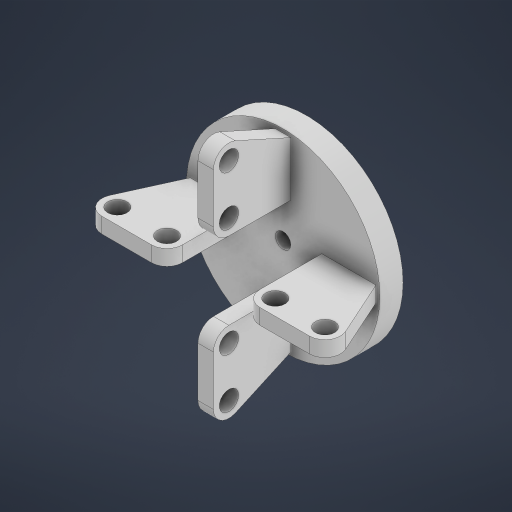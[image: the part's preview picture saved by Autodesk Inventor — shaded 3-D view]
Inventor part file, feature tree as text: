
AUTODESK INVENTOR PART (.ipt)
format: ipt  version: 2023 (Build 270158000, 158)  size: 292,352 bytes
history: native  units: mm
features: extrude x5, sketch x5, pattern_circular x2, fillet x1
ambient origin geometry x8: Origin, YZ Plane, XZ Plane, XY Plane, X Axis, Y Axis, Z Axis, Center Point
bodies: Solid1 (feature_tree)
feature tree (13):
  extrude  "Extrusion1"  Depth=3.0mm TaperAngle=0.0deg
  extrude  "Extrusion2"  Depth=3.0mm TaperAngle=0.0deg
  extrude  "Extrusion3"  Depth=2.0mm TaperAngle=360.0deg
  extrude  "Extrusion5"  Depth=10.0mm
  pattern_circular  "Circular Pattern3"  [2 undecoded]
  fillet  "Fillet2"  Radius=40.0mm
  extrude  "Extrusion6"  Depth=10.0mm
  pattern_circular  "Circular Pattern4"  [2 undecoded]
  sketch  "Sketch1"  dims[d0=25.0mm d1=3.0mm d2=0.0mm]
  sketch  "Sketch2"  dims[d3=2.0mm d4=3.0mm d5=0.0mm]
  sketch  "Sketch3"  dims[d8=2.0mm d9=40.0mm d11=360.0deg]
  sketch  "Sketch5"  dims[d13=10.0mm d14=0.0mm d26=7.0mm]
  sketch  "Sketch6"  dims[d27=10.0mm d28=0.0mm d29=2.0mm d30=40.0mm d31=360.0deg d33=2.5mm d34=2.5mm d35=10.0mm d36=0.0mm d37=40.0mm d38=360.0deg]
note: 4 required parameter values undecoded (feature->parameter linkage not recoverable at this tier; creation-order binding heuristic only, values carry confidence <= 0.55)
